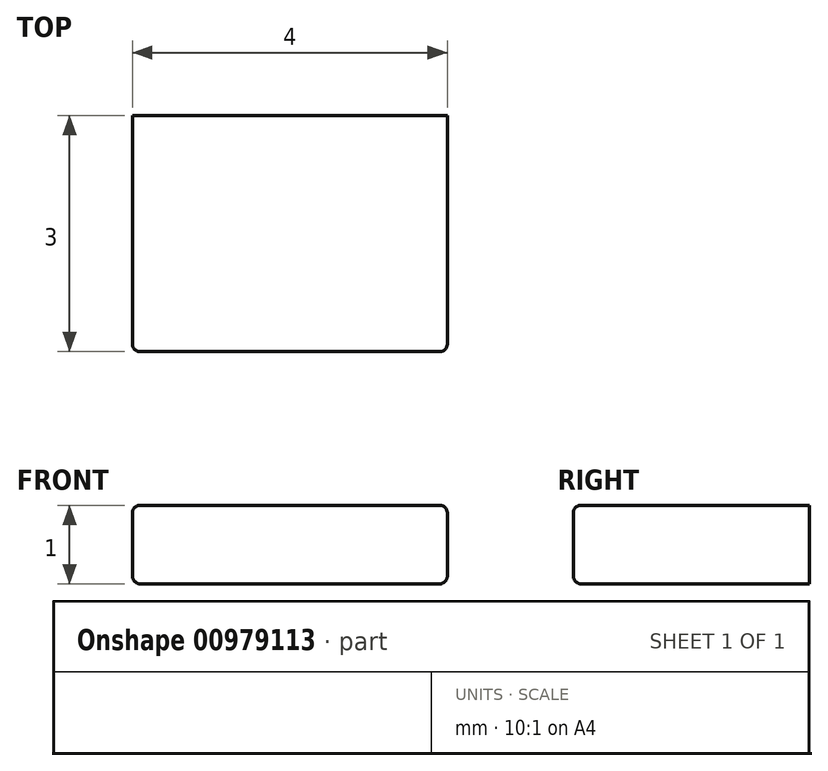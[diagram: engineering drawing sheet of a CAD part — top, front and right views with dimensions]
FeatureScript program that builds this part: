
annotation { "Feature Type Name" : "Feature", "Feature Type Description" : "" }
export const myFeature = defineFeature(function(context is Context, id is Id, definition is map)
    precondition{}
    {
        {
            var Q0;
            Q0=qCreatedBy(makeId("Front.planeOp"),FACE);
            var sketch = newSketch(context, id + "F0", { "sketchPlane" : qUnion([Q0])});
            skLineSegment(sketch, "E0.bottom", {"start": v(2, -0.5) * mm, "end": v(-2, -0.5) * mm});
            skLineSegment(sketch, "E0.top", {"start": v(2, 0.5) * mm, "end": v(-2, 0.5) * mm});
            skLineSegment(sketch, "E0.left", {"start": v(2, -0.5) * mm, "end": v(2, 0.5) * mm});
            skLineSegment(sketch, "E0.right", {"start": v(-2, -0.5) * mm, "end": v(-2, 0.5) * mm});
            skPoint(sketch, "E0.middle", {"position": v(0, 0) * mm});
            skSolve(sketch);
        }
        {
            var Q0;
            Q0 = qSketchRegion(id + "F0", true);
            extrude(context, id + "F1", {"entities" : qUnion([Q0]), "depth" : 2 * mm, "offsetDistance" : 25.4 * mm, "hasSecondDirection" : true, "secondDirectionOppositeDirection" : true, "secondDirectionDepth" : 1 * mm});
        }
        {
            var Q0;
            Q0=makeQuery(id+"F1.opExtrude","SWEPT_EDGE",EDGE,{"disambiguationData":[OSD([sQuery(id+"F0.wireOp",EDGE,"E0.top"),sQuery(id+"F0.wireOp",EDGE,"E0.right")])]});
            var Q1;
            Q1=makeQuery(id+"F1.opExtrude","SWEPT_EDGE",EDGE,{"disambiguationData":[OSD([sQuery(id+"F0.wireOp",EDGE,"E0.top"),sQuery(id+"F0.wireOp",EDGE,"E0.left")])]});
            var Q2;
            Q2=makeQuery(id+"F1.opExtrude","SWEPT_EDGE",EDGE,{"disambiguationData":[OSD([sQuery(id+"F0.wireOp",EDGE,"E0.bottom"),sQuery(id+"F0.wireOp",EDGE,"E0.left")])]});
            var Q3;
            Q3=makeQuery(id+"F1.opExtrude","CAP_EDGE",EDGE,{"disambiguationData":[OSD([sQuery(id+"F0.wireOp",EDGE,"E0.left")])],"isStart":false});
            var Q4;
            Q4=makeQuery(id+"F1.opExtrude","CAP_EDGE",EDGE,{"disambiguationData":[OSD([sQuery(id+"F0.wireOp",EDGE,"E0.top")])],"isStart":false});
            var Q5;
            Q5=makeQuery(id+"F1.opExtrude","CAP_EDGE",EDGE,{"disambiguationData":[OSD([sQuery(id+"F0.wireOp",EDGE,"E0.bottom")])],"isStart":false});
            var Q6;
            Q6=makeQuery(id+"F1.opExtrude","CAP_EDGE",EDGE,{"disambiguationData":[OSD([sQuery(id+"F0.wireOp",EDGE,"E0.right")])],"isStart":false});
            var Q7;
            Q7=makeQuery(id+"F1.opExtrude","SWEPT_EDGE",EDGE,{"disambiguationData":[OSD([sQuery(id+"F0.wireOp",EDGE,"E0.bottom"),sQuery(id+"F0.wireOp",EDGE,"E0.right")])]});
            fillet(context, id + "F2", {"entities" : qUnion([Q0, Q1, Q2, Q3, Q4, Q5, Q6, Q7]), "radius" : .1 * mm, "tangentPropagation" : true, "allowEdgeOverflow" : false});
        }
    });
